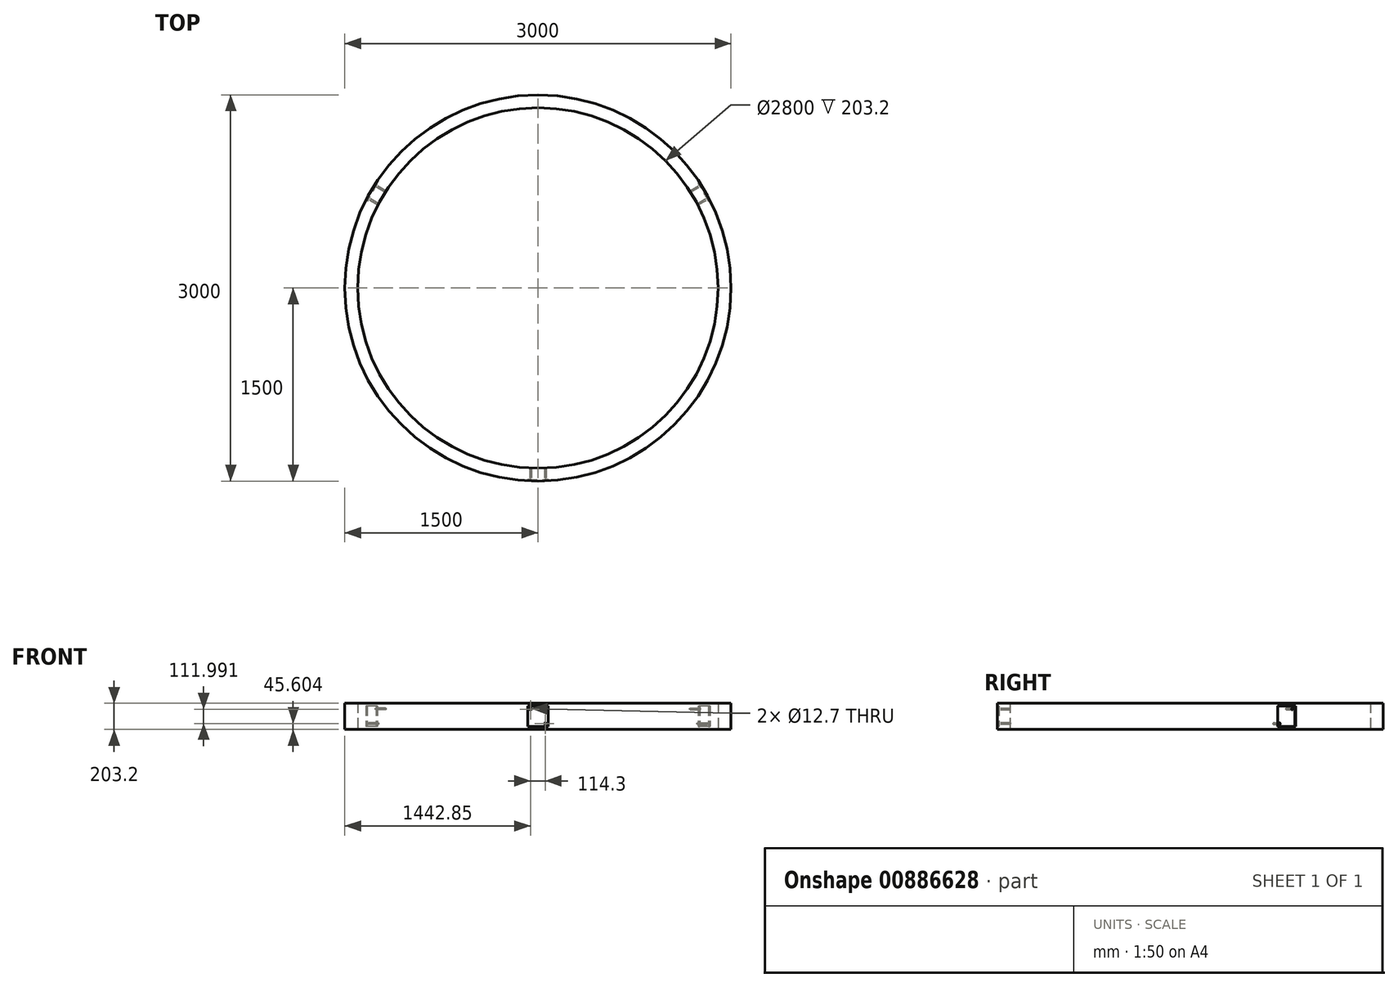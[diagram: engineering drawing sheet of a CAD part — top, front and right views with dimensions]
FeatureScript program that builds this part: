
annotation { "Feature Type Name" : "Feature", "Feature Type Description" : "" }
export const myFeature = defineFeature(function(context is Context, id is Id, definition is map)
    precondition{}
    {
        {
            assignVariable(context, id + "F0", {"name" : "height", "anyValue" : 203.2 * mm});
        }
        {
            var Q0;
            Q0=qCreatedBy(makeId("Top.planeOp"),FACE);
            var sketch = newSketch(context, id + "F1", { "sketchPlane" : qUnion([Q0])});
            skCircle(sketch, "E0", {"center": v(0, 0) * mm, "radius": 1400 * mm});
            skCircle(sketch, "E1", {"center": v(0, 0) * mm, "radius": 1500 * mm});
            skSolve(sketch);
        }
        {
            var Q0;
            Q0=qCreatedBy(makeId("Front.planeOp"),FACE);
            cPlane(context, id + "F2", {"entities" : qUnion([Q0]), "cplaneType" : CPlaneType.OFFSET, "offset" : 2540 * mm, "width" : 152.4 * mm, "height" : 152.4 * mm});
        }
        {
            var Q0;
            Q0=qCreatedBy(makeId("Front.planeOp"),FACE);
            var sketch = newSketch(context, id + "F3", { "sketchPlane" : qUnion([Q0])});
            skLineSegment(sketch, "E2", {"start": v(0, -152.37) * mm, "end": v(0, 154.67) * mm, "construction": true});
            skSolve(sketch);
        }
        {
            var Q0;
            Q0=sQuery(id+"F3.wireOp",EDGE,"E2");
            var Q1;
            Q1=qCreatedBy(makeId("Front.planeOp"),FACE);
            cPlane(context, id + "F4", {"entities" : qUnion([Q0, Q1]), "cplaneType" : CPlaneType.LINE_ANGLE, "offset" : 25.4 * mm, "angle" : 120 * degree, "oppositeDirection" : true, "width" : 152.4 * mm, "height" : 152.4 * mm});
        }
        {
            var Q0;
            Q0=sQuery(id+"F3.wireOp",EDGE,"E2");
            var Q1;
            Q1=qCreatedBy(makeId("Front.planeOp"),FACE);
            cPlane(context, id + "F5", {"entities" : qUnion([Q0, Q1]), "cplaneType" : CPlaneType.LINE_ANGLE, "offset" : 25.4 * mm, "angle" : 240 * degree, "oppositeDirection" : true, "width" : 152.4 * mm, "height" : 152.4 * mm});
        }
        {
            var Q0;
            Q0=qCreatedBy(id+"F4.planeOp",FACE);
            cPlane(context, id + "F6", {"entities" : qUnion([Q0]), "cplaneType" : CPlaneType.OFFSET, "offset" : 2540 * mm, "oppositeDirection" : true, "width" : 152.4 * mm, "height" : 152.4 * mm});
        }
        {
            var Q0;
            Q0=qCreatedBy(id+"F5.planeOp",FACE);
            cPlane(context, id + "F7", {"entities" : qUnion([Q0]), "cplaneType" : CPlaneType.OFFSET, "offset" : 2540 * mm, "oppositeDirection" : true, "width" : 152.4 * mm, "height" : 152.4 * mm});
        }
        {
            var Q0;
            Q0=makeQuery(id+"F1.imprint","IMPRINT",FACE,{"disambiguationData":[TD([[makeQuery(id+"F1.imprint","IMPRINT",EDGE,{"derivedFrom":sQuery(id+"F1.wireOp",EDGE,"E0")}),-1.0]])]});
            extrude(context, id + "F8", {"entities" : qUnion([Q0]), "endBound" : BoundingType.SYMMETRIC, "depth" : getVariable(context, 'height'), "offsetDistance" : 25.4 * mm});
        }
        {
            var Q0;
            Q0=qCreatedBy(id+"F2.planeOp",FACE);
            var sketch = newSketch(context, id + "F9", { "sketchPlane" : qUnion([Q0])});
            skLineSegment(sketch, "E3.bottom", {"start": v(79.38, -79.38) * mm, "end": v(-79.38, -79.38) * mm});
            skLineSegment(sketch, "E3.top", {"start": v(79.38, 79.38) * mm, "end": v(-79.38, 79.38) * mm});
            skLineSegment(sketch, "E3.left", {"start": v(79.38, -79.38) * mm, "end": v(79.38, 79.37) * mm});
            skLineSegment(sketch, "E3.right", {"start": v(-79.38, -79.38) * mm, "end": v(-79.38, 79.37) * mm});
            skPoint(sketch, "E3.middle", {"position": v(0, 0) * mm});
            skSolve(sketch);
        }
        {
            var Q0;
            Q0=makeQuery(id+"F9.imprint","IMPRINT",FACE,{"disambiguationData":[TD([[makeQuery(id+"F9.imprint","IMPRINT",EDGE,{"derivedFrom":sQuery(id+"F9.wireOp",EDGE,"E3.bottom")}),-1.0]])]});
            var Q1;
            Q1=makeQuery(id+"F8.opExtrude","SWEPT_FACE",FACE,{"disambiguationData":[OSD([sQuery(id+"F1.wireOp",EDGE,"E1")])]});
            extrude(context, id + "F10", {"entities" : qUnion([Q0]), "operationType" : NewBodyOperationType.REMOVE, "endBound" : BoundingType.UP_TO_SURFACE, "oppositeDirection" : true, "depth" : 165.1 * mm, "endBoundEntityFace" : qUnion([Q1]), "hasOffset" : true, "offsetDistance" : 12.7 * mm, "offsetOppositeDirection" : true});
        }
        {
            var Q0;
            Q0=qCreatedBy(id+"F6.planeOp",FACE);
            var sketch = newSketch(context, id + "F11", { "sketchPlane" : qUnion([Q0])});
            skLineSegment(sketch, "E4.bottom", {"start": v(-79.38, -79.38) * mm, "end": v(79.38, -79.38) * mm});
            skLineSegment(sketch, "E4.top", {"start": v(-79.38, 79.38) * mm, "end": v(79.37, 79.38) * mm});
            skLineSegment(sketch, "E4.left", {"start": v(-79.38, -79.38) * mm, "end": v(-79.38, 79.38) * mm});
            skLineSegment(sketch, "E4.right", {"start": v(79.38, -79.38) * mm, "end": v(79.37, 79.38) * mm});
            skPoint(sketch, "E4.middle", {"position": v(0, 0) * mm});
            skSolve(sketch);
        }
        {
            var Q0;
            Q0=makeQuery(id+"F11.imprint","IMPRINT",FACE,{"disambiguationData":[TD([[makeQuery(id+"F11.imprint","IMPRINT",EDGE,{"derivedFrom":sQuery(id+"F11.wireOp",EDGE,"E4.bottom")}),1.0]])]});
            var Q1;
            Q1=makeQuery(id+"F8.opExtrude","SWEPT_FACE",FACE,{"disambiguationData":[OSD([sQuery(id+"F1.wireOp",EDGE,"E1")])]});
            extrude(context, id + "F12", {"entities" : qUnion([Q0]), "operationType" : NewBodyOperationType.REMOVE, "endBound" : BoundingType.UP_TO_SURFACE, "depth" : 165.1 * mm, "endBoundEntityFace" : qUnion([Q1]), "hasOffset" : true, "offsetDistance" : 12.7 * mm, "offsetOppositeDirection" : true});
        }
        {
            var Q0;
            Q0=qCreatedBy(id+"F7.planeOp",FACE);
            var sketch = newSketch(context, id + "F13", { "sketchPlane" : qUnion([Q0])});
            skLineSegment(sketch, "E5.bottom", {"start": v(-79.38, -79.38) * mm, "end": v(79.37, -79.38) * mm});
            skLineSegment(sketch, "E5.top", {"start": v(-79.38, 79.38) * mm, "end": v(79.38, 79.38) * mm});
            skLineSegment(sketch, "E5.left", {"start": v(-79.38, -79.38) * mm, "end": v(-79.38, 79.38) * mm});
            skLineSegment(sketch, "E5.right", {"start": v(79.38, -79.38) * mm, "end": v(79.38, 79.38) * mm});
            skPoint(sketch, "E5.middle", {"position": v(0, 0) * mm});
            skSolve(sketch);
        }
        {
            var Q0;
            Q0=makeQuery(id+"F13.imprint","IMPRINT",FACE,{"disambiguationData":[TD([[makeQuery(id+"F13.imprint","IMPRINT",EDGE,{"derivedFrom":sQuery(id+"F13.wireOp",EDGE,"E5.bottom")}),1.0]])]});
            var Q1;
            Q1=makeQuery(id+"F8.opExtrude","SWEPT_FACE",FACE,{"disambiguationData":[OSD([sQuery(id+"F1.wireOp",EDGE,"E1")])]});
            extrude(context, id + "F14", {"entities" : qUnion([Q0]), "operationType" : NewBodyOperationType.REMOVE, "endBound" : BoundingType.UP_TO_SURFACE, "depth" : 165.1 * mm, "endBoundEntityFace" : qUnion([Q1]), "hasOffset" : true, "offsetDistance" : 12.7 * mm, "offsetOppositeDirection" : true});
        }
        {
            var Q0;
            Q0=qCreatedBy(id+"F7.planeOp",FACE);
            var sketch = newSketch(context, id + "F15", { "sketchPlane" : qUnion([Q0])});
            skCircle(sketch, "E6", {"center": v(-57.15, 57.15) * mm, "radius": 6.35 * mm});
            skLineSegment(sketch, "E7", {"start": v(-108.03, 0) * mm, "end": v(124.77, 0) * mm, "construction": true});
            skCircle(sketch, "E8.MirrorC", {"center": v(57.15, 57.15) * mm, "radius": 6.35 * mm});
            skCircle(sketch, "E9.MirrorC", {"center": v(-57.15, -57.15) * mm, "radius": 6.35 * mm});
            skCircle(sketch, "E10.MirrorC", {"center": v(57.15, -57.15) * mm, "radius": 6.35 * mm});
            skSolve(sketch);
        }
        {
            var Q0;
            Q0=makeQuery(id+"F15.imprint","IMPRINT",FACE,{"disambiguationData":[TD([[makeQuery(id+"F15.imprint","IMPRINT",EDGE,{"derivedFrom":sQuery(id+"F15.wireOp",EDGE,"E9.MirrorC")}),-1.0]])]});
            var Q1;
            Q1=makeQuery(id+"F15.imprint","IMPRINT",FACE,{"disambiguationData":[TD([[makeQuery(id+"F15.imprint","IMPRINT",EDGE,{"derivedFrom":sQuery(id+"F15.wireOp",EDGE,"E6")}),1.0]])]});
            var Q2;
            Q2=makeQuery(id+"F15.imprint","IMPRINT",FACE,{"disambiguationData":[TD([[makeQuery(id+"F15.imprint","IMPRINT",EDGE,{"derivedFrom":sQuery(id+"F15.wireOp",EDGE,"E8.MirrorC")}),-1.0]])]});
            var Q3;
            Q3=makeQuery(id+"F15.imprint","IMPRINT",FACE,{"disambiguationData":[TD([[makeQuery(id+"F15.imprint","IMPRINT",EDGE,{"derivedFrom":sQuery(id+"F15.wireOp",EDGE,"E10.MirrorC")}),1.0]])]});
            var Q4;
            Q4=makeQuery(id+"F8.opExtrude","SWEPT_FACE",FACE,{"disambiguationData":[OSD([sQuery(id+"F1.wireOp",EDGE,"E1")])]});
            extrude(context, id + "F16", {"entities" : qUnion([Q0, Q1, Q2, Q3]), "operationType" : NewBodyOperationType.REMOVE, "endBound" : BoundingType.UP_TO_SURFACE, "depth" : 254 * mm, "endBoundEntityFace" : qUnion([Q4]), "hasOffset" : true, "offsetDistance" : 152.4 * mm, "offsetOppositeDirection" : true});
        }
        {
            var Q0;
            Q0=qCreatedBy(id+"F6.planeOp",FACE);
            var sketch = newSketch(context, id + "F17", { "sketchPlane" : qUnion([Q0])});
            skCircle(sketch, "E11", {"center": v(-57.15, -57.15) * mm, "radius": 6.35 * mm});
            skLineSegment(sketch, "E12", {"start": v(-161.08, 0) * mm, "end": v(125.39, 0) * mm, "construction": true});
            skCircle(sketch, "E13.MirrorC", {"center": v(-57.15, 57.15) * mm, "radius": 6.35 * mm});
            skCircle(sketch, "E14.MirrorC", {"center": v(57.15, 57.15) * mm, "radius": 6.35 * mm});
            skCircle(sketch, "E15.MirrorC", {"center": v(57.15, -57.15) * mm, "radius": 6.35 * mm});
            skSolve(sketch);
        }
        {
            var Q0;
            Q0=makeQuery(id+"F17.imprint","IMPRINT",FACE,{"disambiguationData":[TD([[makeQuery(id+"F17.imprint","IMPRINT",EDGE,{"derivedFrom":sQuery(id+"F17.wireOp",EDGE,"E11")}),1.0]])]});
            var Q1;
            Q1=makeQuery(id+"F17.imprint","IMPRINT",FACE,{"disambiguationData":[TD([[makeQuery(id+"F17.imprint","IMPRINT",EDGE,{"derivedFrom":sQuery(id+"F17.wireOp",EDGE,"E13.MirrorC")}),-1.0]])]});
            var Q2;
            Q2=makeQuery(id+"F17.imprint","IMPRINT",FACE,{"disambiguationData":[TD([[makeQuery(id+"F17.imprint","IMPRINT",EDGE,{"derivedFrom":sQuery(id+"F17.wireOp",EDGE,"E14.MirrorC")}),1.0]])]});
            var Q3;
            Q3=makeQuery(id+"F17.imprint","IMPRINT",FACE,{"disambiguationData":[TD([[makeQuery(id+"F17.imprint","IMPRINT",EDGE,{"derivedFrom":sQuery(id+"F17.wireOp",EDGE,"E15.MirrorC")}),-1.0]])]});
            var Q4;
            Q4=makeQuery(id+"F8.opExtrude","SWEPT_FACE",FACE,{"disambiguationData":[OSD([sQuery(id+"F1.wireOp",EDGE,"E1")])]});
            extrude(context, id + "F18", {"entities" : qUnion([Q0, Q1, Q2, Q3]), "operationType" : NewBodyOperationType.REMOVE, "endBound" : BoundingType.UP_TO_SURFACE, "depth" : 254 * mm, "endBoundEntityFace" : qUnion([Q4]), "hasOffset" : true, "offsetDistance" : 152.4 * mm, "offsetOppositeDirection" : true});
        }
        {
            var Q0;
            Q0=qCreatedBy(id+"F2.planeOp",FACE);
            var sketch = newSketch(context, id + "F19", { "sketchPlane" : qUnion([Q0])});
            skCircle(sketch, "E16", {"center": v(57.15, -56) * mm, "radius": 6.35 * mm});
            skLineSegment(sketch, "E17", {"start": v(130.32, 0) * mm, "end": v(-113.55, 0) * mm, "construction": true});
            skCircle(sketch, "E18.MirrorC", {"center": v(57.15, 56) * mm, "radius": 6.35 * mm});
            skCircle(sketch, "E19.MirrorC", {"center": v(-57.15, 56) * mm, "radius": 6.35 * mm});
            skCircle(sketch, "E20.MirrorC", {"center": v(-57.15, -56) * mm, "radius": 6.35 * mm});
            skSolve(sketch);
        }
        {
            var Q0;
            Q0=makeQuery(id+"F19.imprint","IMPRINT",FACE,{"disambiguationData":[TD([[makeQuery(id+"F19.imprint","IMPRINT",EDGE,{"derivedFrom":sQuery(id+"F19.wireOp",EDGE,"E19.MirrorC")}),1.0]])]});
            var Q1;
            Q1=makeQuery(id+"F19.imprint","IMPRINT",FACE,{"disambiguationData":[TD([[makeQuery(id+"F19.imprint","IMPRINT",EDGE,{"derivedFrom":sQuery(id+"F19.wireOp",EDGE,"E18.MirrorC")}),-1.0]])]});
            var Q2;
            Q2=makeQuery(id+"F19.imprint","IMPRINT",FACE,{"disambiguationData":[TD([[makeQuery(id+"F19.imprint","IMPRINT",EDGE,{"derivedFrom":sQuery(id+"F19.wireOp",EDGE,"E16")}),1.0]])]});
            var Q3;
            Q3=makeQuery(id+"F19.imprint","IMPRINT",FACE,{"disambiguationData":[TD([[makeQuery(id+"F19.imprint","IMPRINT",EDGE,{"derivedFrom":sQuery(id+"F19.wireOp",EDGE,"E20.MirrorC")}),-1.0]])]});
            var Q4;
            Q4=makeQuery(id+"F8.opExtrude","SWEPT_FACE",FACE,{"disambiguationData":[OSD([sQuery(id+"F1.wireOp",EDGE,"E1")])]});
            extrude(context, id + "F20", {"entities" : qUnion([Q0, Q1, Q2, Q3]), "operationType" : NewBodyOperationType.REMOVE, "endBound" : BoundingType.UP_TO_SURFACE, "oppositeDirection" : true, "depth" : 254 * mm, "endBoundEntityFace" : qUnion([Q4]), "hasOffset" : true, "offsetDistance" : 152.4 * mm, "offsetOppositeDirection" : true});
        }
    });
